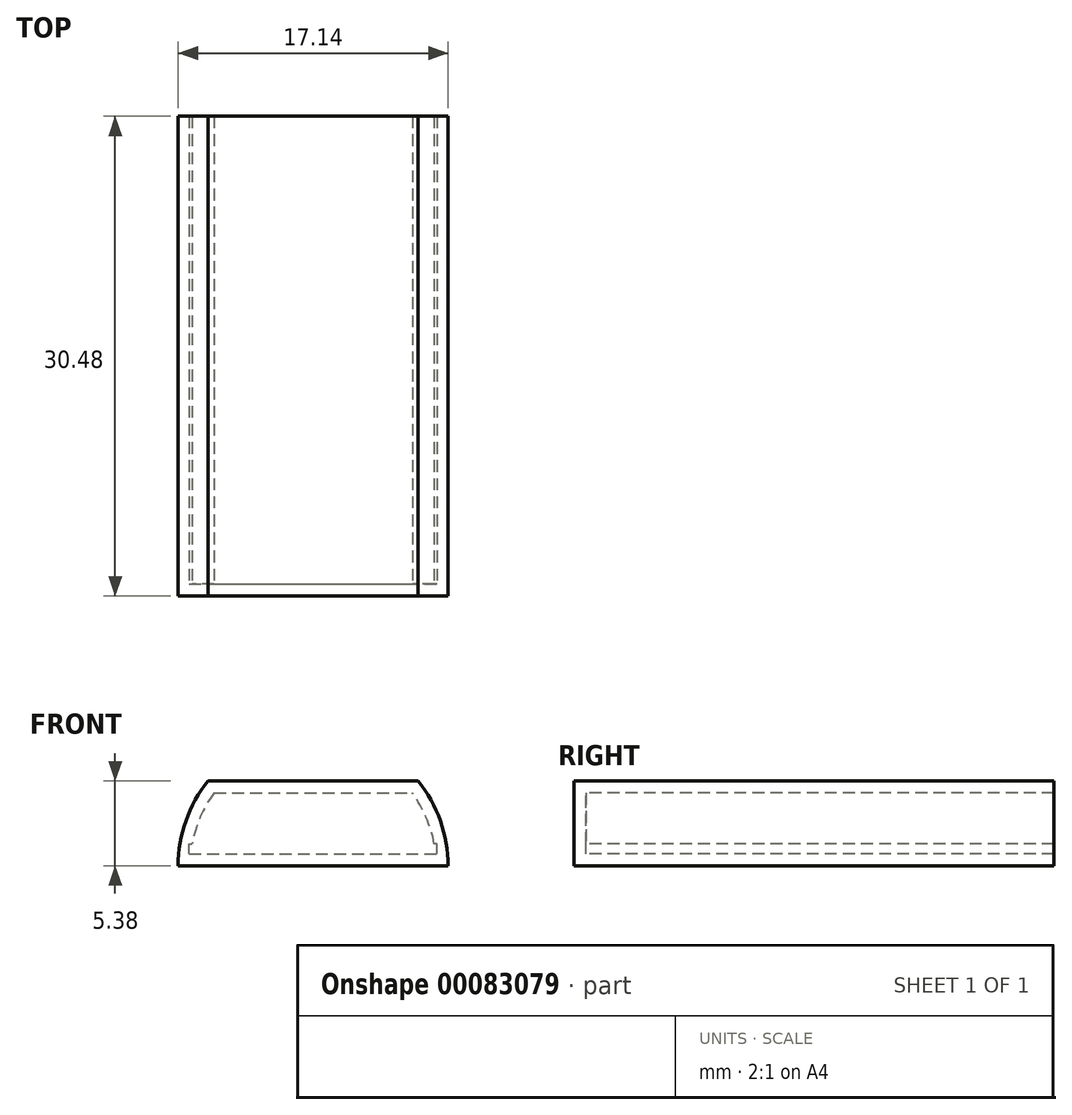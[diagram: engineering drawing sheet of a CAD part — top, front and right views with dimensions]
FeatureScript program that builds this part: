
annotation { "Feature Type Name" : "Feature", "Feature Type Description" : "" }
export const myFeature = defineFeature(function(context is Context, id is Id, definition is map)
    precondition{}
    {
        {
            var Q0;
            Q0=qCreatedBy(makeId("Front.planeOp"),FACE);
            var sketch = newSketch(context, id + "F0", { "sketchPlane" : qUnion([Q0])});
            skArc(sketch, "E0", {"start": v(8.57, 0) * mm, "mid": v(8.08, 2.86) * mm, "end": v(6.67, 5.38) * mm});
            skLineSegment(sketch, "E1", {"start": v(8.57, 0) * mm, "end": v(-8.57, 0) * mm});
            skLineSegment(sketch, "E2", {"start": v(-6.67, 5.38) * mm, "end": v(6.67, 5.38) * mm});
            skArc(sketch, "E3.trimOffspring", {"start": v(-6.67, 5.38) * mm, "mid": v(-8.08, 2.86) * mm, "end": v(-8.57, 0) * mm});
            skLineSegment(sketch, "E4.0", {"start": v(-6.3, 4.62) * mm, "end": v(6.3, 4.62) * mm});
            skArc(sketch, "E4.1", {"start": v(-6.3, 4.62) * mm, "mid": v(-7.17, 3.09) * mm, "end": v(-7.68, 1.4) * mm});
            skLineSegment(sketch, "E4.2", {"start": v(7.77, 0.76) * mm, "end": v(-7.77, 0.76) * mm});
            skArc(sketch, "E4.3", {"start": v(7.69, 1.38) * mm, "mid": v(7.18, 3.08) * mm, "end": v(6.3, 4.62) * mm});
            skLineSegment(sketch, "E5", {"start": v(-7.87, 0.76) * mm, "end": v(-7.87, 1.4) * mm});
            skLineSegment(sketch, "E6", {"start": v(7.87, 0.76) * mm, "end": v(7.87, 1.38) * mm});
            skLineSegment(sketch, "E7", {"start": v(-7.87, 0.76) * mm, "end": v(7.87, 0.76) * mm});
            skLineSegment(sketch, "E8", {"start": v(-7.87, 1.4) * mm, "end": v(-7.68, 1.4) * mm});
            skLineSegment(sketch, "E9", {"start": v(7.87, 1.38) * mm, "end": v(7.69, 1.38) * mm});
            skSolve(sketch);
        }
        {
            var Q0;
            Q0=makeQuery(id+"F0.imprint","IMPRINT",FACE,{"disambiguationData":[TD([[makeQuery(id+"F0.imprint","IMPRINT",EDGE,{"derivedFrom":sQuery(id+"F0.wireOp",EDGE,"E0")}),1.0]])]});
            extrude(context, id + "F1", {"entities" : qUnion([Q0]), "oppositeDirection" : true, "depth" : 30.48 * mm});
        }
        {
            var Q0;
            Q0=makeQuery(id+"F1.opExtrude","CAP_FACE",FACE,{"disambiguationData":[OSD([sQuery(id+"F0.wireOp",EDGE,"E0"),sQuery(id+"F0.wireOp",EDGE,"E1"),sQuery(id+"F0.wireOp",EDGE,"E2"),sQuery(id+"F0.wireOp",EDGE,"E3.trimOffspring"),sQuery(id+"F0.wireOp",EDGE,"E4.0"),sQuery(id+"F0.wireOp",EDGE,"E4.1"),sQuery(id+"F0.wireOp",EDGE,"E4.3"),sQuery(id+"F0.wireOp",EDGE,"E5"),sQuery(id+"F0.wireOp",EDGE,"E6"),sQuery(id+"F0.wireOp",EDGE,"E7"),sQuery(id+"F0.wireOp",EDGE,"E8"),sQuery(id+"F0.wireOp",EDGE,"E9")])],"isStart":true});
            var sketch = newSketch(context, id + "F2", { "sketchPlane" : qUnion([Q0])});
            skLineSegment(sketch, "E10.0.0", {"start": v(-8.57, 0) * mm, "end": v(8.57, 0) * mm, "construction": true});
            skArc(sketch, "E10.0.1", {"start": v(8.57, 0) * mm, "mid": v(8.08, 2.86) * mm, "end": v(6.67, 5.38) * mm, "construction": true});
            skLineSegment(sketch, "E10.0.2", {"start": v(6.67, 5.38) * mm, "end": v(-6.67, 5.38) * mm, "construction": true});
            skArc(sketch, "E10.0.3", {"start": v(-6.67, 5.38) * mm, "mid": v(-8.08, 2.86) * mm, "end": v(-8.57, 0) * mm, "construction": true});
            skLineSegment(sketch, "E11.0", {"start": v(-6.3, 4.62) * mm, "end": v(6.3, 4.62) * mm, "construction": true});
            skLineSegment(sketch, "E12.0", {"start": v(-7.87, 0.76) * mm, "end": v(7.87, 0.76) * mm, "construction": true});
            skLineSegment(sketch, "E13.0", {"start": v(-7.87, 0.76) * mm, "end": v(-7.87, 1.4) * mm, "construction": true});
            skLineSegment(sketch, "E14.0", {"start": v(-7.87, 1.4) * mm, "end": v(-7.68, 1.4) * mm, "construction": true});
            skArc(sketch, "E15.0", {"start": v(-6.3, 4.62) * mm, "mid": v(-7.17, 3.09) * mm, "end": v(-7.68, 1.4) * mm, "construction": true});
            skArc(sketch, "E16.0", {"start": v(7.69, 1.38) * mm, "mid": v(7.18, 3.08) * mm, "end": v(6.3, 4.62) * mm, "construction": true});
            skLineSegment(sketch, "E17.0", {"start": v(7.87, 1.38) * mm, "end": v(7.69, 1.38) * mm, "construction": true});
            skLineSegment(sketch, "E18.0", {"start": v(7.87, 0.76) * mm, "end": v(7.87, 1.38) * mm, "construction": true});
            skSolve(sketch);
        }
        {
            var Q0;
            Q0=makeQuery(id+"F2.imprint","IMPRINT",FACE,{"disambiguationData":[TD([[makeQuery(id+"F2.imprint","IMPRINT",EDGE,{"derivedFrom":makeQuery(id+"F1.opExtrude","CAP_EDGE",EDGE,{"disambiguationData":[OSD([sQuery(id+"F0.wireOp",EDGE,"E4.0")])],"isStart":true})}),-1.0]])]});
            extrude(context, id + "F3", {"entities" : qUnion([Q0]), "operationType" : NewBodyOperationType.ADD, "oppositeDirection" : true, "depth" : 0.76 * mm});
        }
    });
